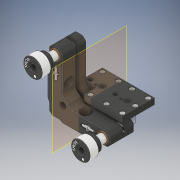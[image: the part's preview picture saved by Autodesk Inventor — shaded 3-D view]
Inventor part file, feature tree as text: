
AUTODESK INVENTOR PART (.ipt)
format: ipt  version: 2019 (Build 230136000, 136)  size: 3,251,200 bytes
history: native  units: in
note: dims shown in document units (in); Inventor stores cm internally (conversion verified against a paired STEP export)
features: other x28, plane x1
ambient origin geometry x8: Origin, YZ Plane, XZ Plane, XY Plane, X Axis, Y Axis, Z Axis, Center Point
bodies: Solid1 (feature_tree), Solid2 (feature_tree), Solid3 (feature_tree), Solid4 (feature_tree), Solid5 (feature_tree), Solid6 (feature_tree), Solid7 (feature_tree), Solid8 (feature_tree), Solid9 (feature_tree), Solid10 (feature_tree), Solid11 (feature_tree), Solid12 (feature_tree), Solid13 (feature_tree), Solid14 (feature_tree), Solid15 (feature_tree), Solid16 (feature_tree), Solid17 (feature_tree), Solid18 (feature_tree), Solid19 (feature_tree), Solid20 (feature_tree), Solid21 (feature_tree), Solid22 (feature_tree), Solid23 (feature_tree), Solid24 (feature_tree), Solid25 (feature_tree), Solid26 (feature_tree), Solid27 (feature_tree), Solid28 (feature_tree)
feature tree (29):
  plane  "Work Plane1"
  other  "6628-001-1-solid1"
  other  "6631-003-1-solid1"
  other  "0017-002-1-solid1"
  other  "0017-002-2-solid1"
  other  "W25H042-1-solid1"
  other  "DOWEL0625X250-3-solid1"
  other  "DOWEL0625X250-4-solid1"
  other  "0806-001-1-solid1"
  other  "0806-001-2-solid1"
  other  "1579-004-1-solid1"
  other  "1579-004-2-solid1"
  other  "BALL3125GR100-1-solid1"
  other  "BALL1875GR100-1-solid1"
  other  "BALL1875GR100-2-solid1"
  other  "KM2 SPRING ASSY-1_SPRG-KM1-1-solid1"
  other  "KM2 SPRING ASSY-1_SS6S025-1-1-solid1"
  other  "KM2 SPRING ASSY-2_SPRG-KM1-1-solid1"
  other  "KM2 SPRING ASSY-2_SS6S025-1-1-solid1"
  other  "DOWEL0625X375-1-solid1"
  other  "DOWEL0625X375-2-solid1"
  other  "SH3A019-1-3-solid1"
  other  "SH3A019-1-4-solid1"
  other  "DOWEL0625X250-8-solid1"
  other  "TTN005949-1-solid1"
  other  "TTN005977-1-solid1"
  other  "SH4A025-1-1-solid1"
  other  "SH4A025-1-2-solid1"
  other  "DOWEL0625X250-9-solid1"
